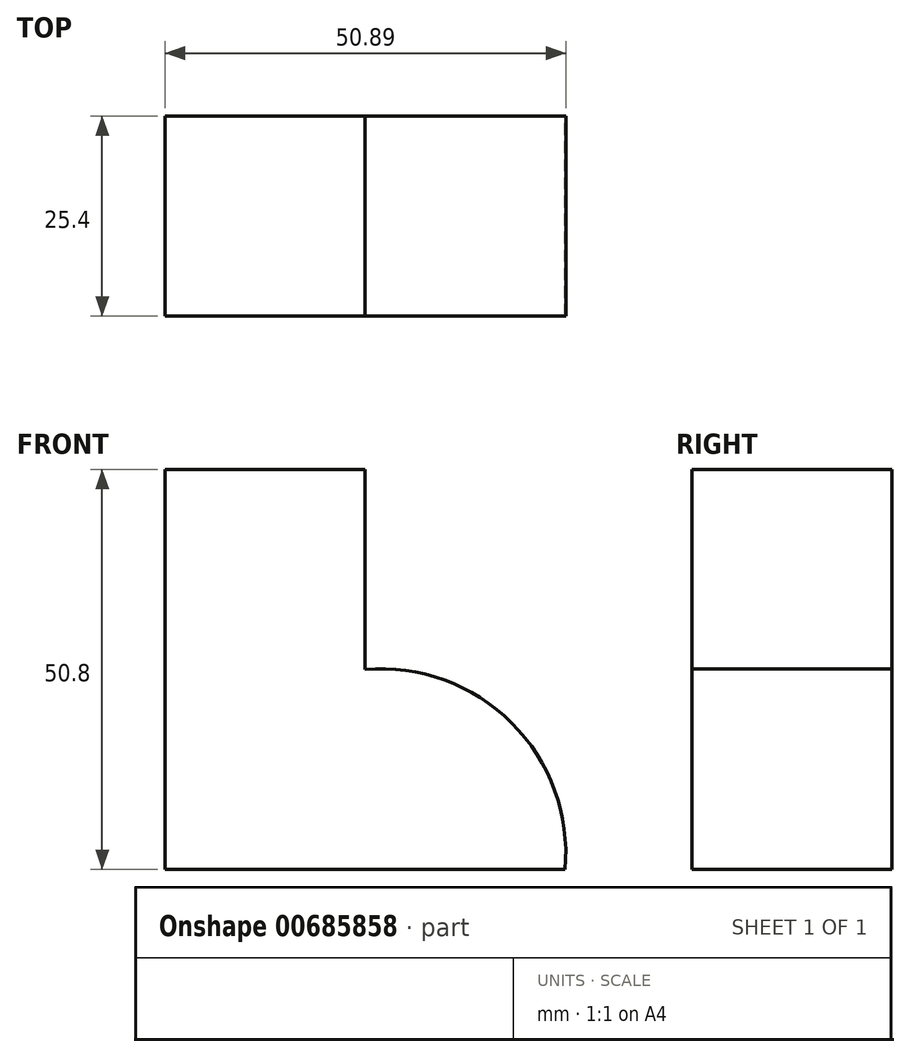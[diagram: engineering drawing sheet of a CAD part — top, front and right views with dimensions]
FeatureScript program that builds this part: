
annotation { "Feature Type Name" : "Feature", "Feature Type Description" : "" }
export const myFeature = defineFeature(function(context is Context, id is Id, definition is map)
    precondition{}
    {
        {
            var Q0;
            Q0=qCreatedBy(makeId("Front.planeOp"),FACE);
            var sketch = newSketch(context, id + "F0", { "sketchPlane" : qUnion([Q0])});
            skLineSegment(sketch, "E0", {"start": v(-25.4, 18.05) * mm, "end": v(-25.4, -32.75) * mm});
            skLineSegment(sketch, "E1", {"start": v(-25.4, 18.05) * mm, "end": v(0, 18.05) * mm});
            skLineSegment(sketch, "E2", {"start": v(-25.4, -32.75) * mm, "end": v(25.4, -32.75) * mm});
            skLineSegment(sketch, "E3", {"start": v(0, 18.05) * mm, "end": v(0, -7.35) * mm});
            skArc(sketch, "E4", {"start": v(25.4, -32.75) * mm, "mid": v(18.6, -14.14) * mm, "end": v(0, -7.35) * mm});
            skSolve(sketch);
        }
        {
            var Q0;
            Q0 = qSketchRegion(id + "F0", true);
            extrude(context, id + "F1", {"entities" : qUnion([Q0]), "depth" : 25.4 * mm, "offsetDistance" : 25.4 * mm});
        }
    });
